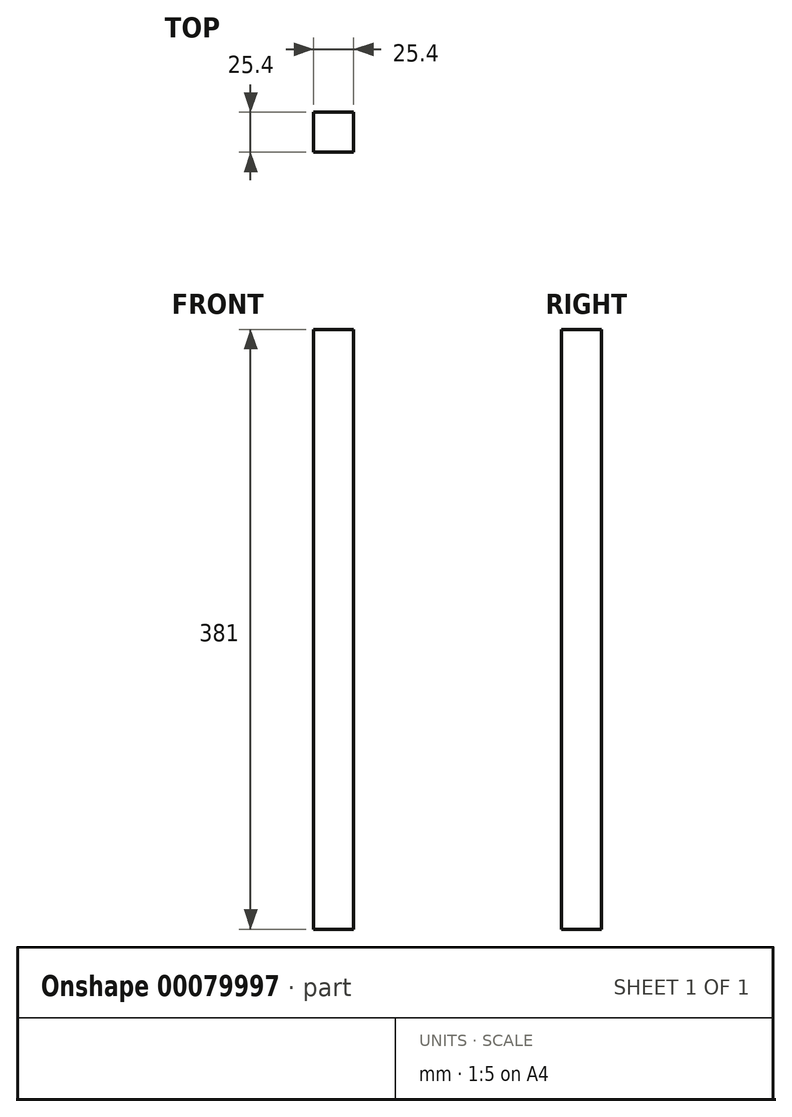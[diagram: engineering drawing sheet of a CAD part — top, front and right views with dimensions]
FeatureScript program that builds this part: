
annotation { "Feature Type Name" : "Feature", "Feature Type Description" : "" }
export const myFeature = defineFeature(function(context is Context, id is Id, definition is map)
    precondition{}
    {
        {
            var Q0;
            Q0=qCreatedBy(makeId("Top.planeOp"),FACE);
            var sketch = newSketch(context, id + "F0", { "sketchPlane" : qUnion([Q0])});
            skLineSegment(sketch, "E0.bottom", {"start": v(12.7, -12.7) * mm, "end": v(-12.7, -12.7) * mm});
            skLineSegment(sketch, "E0.top", {"start": v(12.7, 12.7) * mm, "end": v(-12.7, 12.7) * mm});
            skLineSegment(sketch, "E0.left", {"start": v(12.7, -12.7) * mm, "end": v(12.7, 12.7) * mm});
            skLineSegment(sketch, "E0.right", {"start": v(-12.7, -12.7) * mm, "end": v(-12.7, 12.7) * mm});
            skPoint(sketch, "E0.middle", {"position": v(0, 0) * mm});
            skSolve(sketch);
        }
        {
            var Q0;
            Q0=makeQuery(id+"F0.imprint","IMPRINT",FACE,{"disambiguationData":[TD([[makeQuery(id+"F0.imprint","IMPRINT",EDGE,{"derivedFrom":sQuery(id+"F0.wireOp",EDGE,"E0.bottom")}),-1.0]])]});
            extrude(context, id + "F1", {"entities" : qUnion([Q0]), "depth" : 381 * mm});
        }
    });
